# Revit family: Doors - Hardware_Door_Dormakaba_TS98XEA
name_source: partatom
category: Allgemeines Modell
revit_build: Autodesk Revit 2016 (Build: 20150220_1215(x64)
units: mm (PartAtom-declared; Revit-internal decimal feet)

## family parameters
Basisbauteil = Fläche
Beim Laden mit Abzugskörper schneiden = Nein
Bemaßung runder Anschluss = Durchmesser verwenden
Gemeinsam genutzt = Nein
Kann Basisbauteil für Bewehrung sein = Nein
OmniClass-Nummer = 23.30.40.11.27.11
OmniClass-Titel = Door Closers
Raumberechnungspunkt = Nein
Teiletyp = Normal

## types (1)
- Doors - Hardware_Door_Dormakaba_TS98XEA
    Brand url = http://www.dormakaba.com
    Depth Jamb to Door = 0 mm  [stored 0 ft]
    Design country = Germany
    Door Closers Types = TS 98 XEA_Push-Side-Door_Fixing
    Edition number = 1
    Front Position Closer Height = 83 mm  [stored 0.27231 ft]
    Manufacturer country = Germany
    Manufacturer name = DORMA
    Material main = Cast iron
    Material secondary = Steel
    NBS Reference Code = 25-38-20-20
    NBS Reference Description = Door Hardware Systems
    Nominal height = 60 mm  [stored 0.19685 ft]
    Nominal width = 327 mm
    OmniClass Code = 23-17 19 11 19 11
    OmniClass Description = Door Closers
    Opening Angle = 0.00°
    Primary Material = Aluminium-Dormkaba-Anodized Silver
    Product SKU = ts_98_xea_en_1-6
    Product url = http://www.dorma.com
    Pull Side Door = TS 98 XEA_Pull-Side-Door_Fixing
    Pull side Transom = TS 98 XEA_Pull-Side-Transom-Fixing
    Push Side Door = TS 98 XEA_Push-Side-Door_Fixing
    Push Side Transom = TS 98 XEA_Push-Side-Transom_Fixing
    Uniclass 1.4 Code = L41812
    Uniclass 1.4 Description = Door closers
    Uniclass 2015 Code = Pr_30_36_59_92
    Uniclass 2015 Name = Uncontrolled door closers
    Vorgabe-Ansicht = 1219 mm
    Weight Net (Kg) = 4

note: [stored X ft] marks values corroborated as IEEE doubles in the binary element streams (Revit-internal decimal feet)

## geometry (parser evidence)
native form markers: Blend x2, Sweep x26
no freeform markers — native parametric forms only
